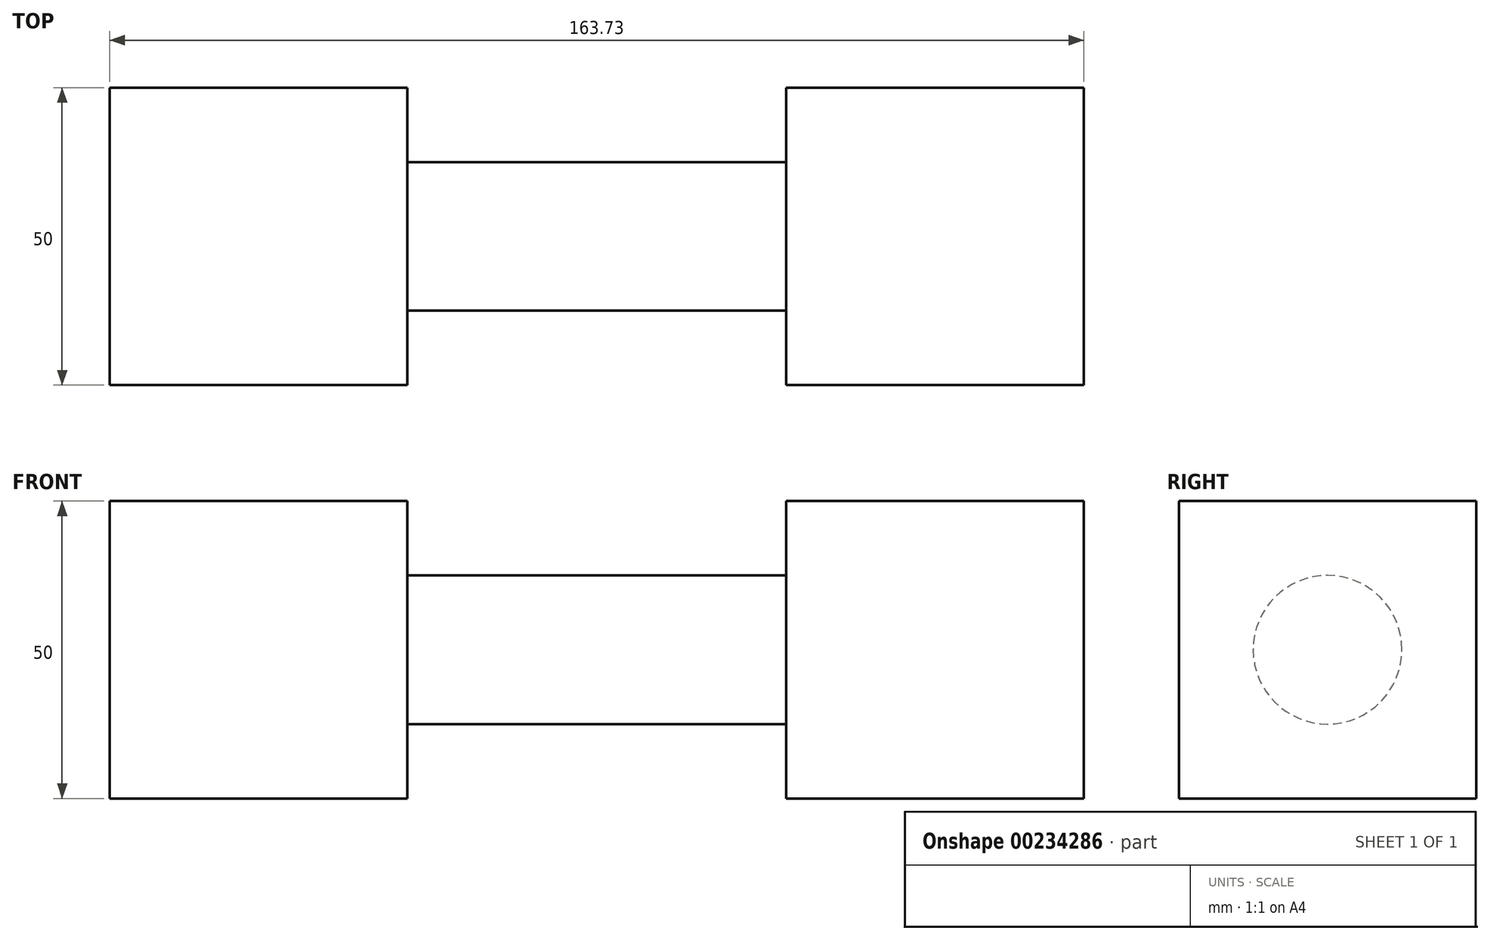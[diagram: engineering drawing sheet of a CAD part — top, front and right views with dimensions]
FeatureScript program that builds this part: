
annotation { "Feature Type Name" : "Feature", "Feature Type Description" : "" }
export const myFeature = defineFeature(function(context is Context, id is Id, definition is map)
    precondition{}
    {
        {
            var Q0;
            Q0=qCreatedBy(makeId("Top.planeOp"),FACE);
            var sketch = newSketch(context, id + "F0", { "sketchPlane" : qUnion([Q0])});
            skLineSegment(sketch, "E0.bottom", {"start": v(-67.16, 62.12) * mm, "end": v(-17.16, 62.12) * mm});
            skLineSegment(sketch, "E0.top", {"start": v(-67.16, 12.12) * mm, "end": v(-17.16, 12.12) * mm});
            skLineSegment(sketch, "E0.left", {"start": v(-67.16, 62.12) * mm, "end": v(-67.16, 12.12) * mm});
            skLineSegment(sketch, "E0.right", {"start": v(-17.16, 62.12) * mm, "end": v(-17.16, 12.12) * mm});
            skSolve(sketch);
        }
        {
            var Q0;
            Q0=makeQuery(id+"F0.imprint","IMPRINT",FACE,{"disambiguationData":[TD([[makeQuery(id+"F0.imprint","IMPRINT",EDGE,{"derivedFrom":sQuery(id+"F0.wireOp",EDGE,"E0.bottom")}),-1.0]])]});
            extrude(context, id + "F1", {"entities" : qUnion([Q0]), "depth" : 50 * mm});
        }
        {
            var Q0;
            Q0=qCreatedBy(makeId("Top.planeOp"),FACE);
            var sketch = newSketch(context, id + "F2", { "sketchPlane" : qUnion([Q0])});
            skPoint(sketch, "E1.0.end.orphan", {"position": v(-17.16, 12.12) * mm});
            skPoint(sketch, "E1.0.start.orphan", {"position": v(-17.16, 62.12) * mm});
            skLineSegment(sketch, "E2.bottom", {"start": v(46.57, 62.12) * mm, "end": v(96.57, 62.12) * mm});
            skLineSegment(sketch, "E2.top", {"start": v(46.57, 12.12) * mm, "end": v(96.57, 12.12) * mm});
            skLineSegment(sketch, "E2.left", {"start": v(46.57, 62.12) * mm, "end": v(46.57, 12.12) * mm});
            skLineSegment(sketch, "E2.right", {"start": v(96.57, 62.12) * mm, "end": v(96.57, 12.12) * mm});
            skSolve(sketch);
        }
        {
            var Q0;
            Q0=makeQuery(id+"F2.imprint","IMPRINT",FACE,{"disambiguationData":[TD([[makeQuery(id+"F2.imprint","IMPRINT",EDGE,{"derivedFrom":sQuery(id+"F2.wireOp",EDGE,"E2.bottom")}),-1.0]])]});
            var Q1;
            Q1=makeQuery(id+"F1.opExtrude","CAP_FACE",FACE,{"disambiguationData":[OSD([sQuery(id+"F0.wireOp",EDGE,"E0.bottom"),sQuery(id+"F0.wireOp",EDGE,"E0.top"),sQuery(id+"F0.wireOp",EDGE,"E0.left"),sQuery(id+"F0.wireOp",EDGE,"E0.right")])],"isStart":false});
            extrude(context, id + "F3", {"entities" : qUnion([Q0]), "endBound" : BoundingType.UP_TO_SURFACE, "endBoundEntityFace" : qUnion([Q1]), "depth" : 25 * mm});
        }
        {
            var Q0;
            Q0=makeQuery(id+"F1.opExtrude","SWEPT_FACE",FACE,{"disambiguationData":[OSD([sQuery(id+"F0.wireOp",EDGE,"E0.right")])]});
            var sketch = newSketch(context, id + "F4", { "sketchPlane" : qUnion([Q0])});
            skPoint(sketch, "E3", {"position": v(62.12, 25) * mm});
            skPoint(sketch, "E4", {"position": v(37.12, 50) * mm});
            skCircle(sketch, "E5", {"center": v(37.12, 25) * mm, "radius": 12.5 * mm});
            skSolve(sketch);
        }
        {
            var Q0;
            Q0=makeQuery(id+"F4.imprint","IMPRINT",FACE,{"disambiguationData":[TD([[makeQuery(id+"F4.imprint","IMPRINT",EDGE,{"derivedFrom":sQuery(id+"F4.wireOp",EDGE,"E5")}),1.0]])]});
            var Q1;
            Q1=makeQuery(id+"F3.opExtrude","SWEPT_FACE",FACE,{"disambiguationData":[OSD([sQuery(id+"F2.wireOp",EDGE,"E2.left")])]});
            extrude(context, id + "F5", {"entities" : qUnion([Q0]), "operationType" : NewBodyOperationType.ADD, "endBound" : BoundingType.UP_TO_SURFACE, "endBoundEntityFace" : qUnion([Q1]), "depth" : 25 * mm});
        }
    });
